# Revit family: Furniture_Sofas-Armchairs_HAGS_Armrest_sofa_armchair_couples
name_source: partatom
category: Furniture
revit_build: Autodesk Revit 2018 (Build: 20170223_1515(x64)
units: mm (PartAtom-declared; Revit-internal decimal feet)

## family parameters
Always vertical = Yes
Cut with Voids When Loaded = No
OmniClass Number = 23.21.23.13.15
OmniClass Title = Residential Sofas
Room Calculation Point = No
Shared = No
Work Plane-Based = No

## types (2) — shared parameters
BIMobject category = Sofas & Armchairs
Description = Armrest sofa / armchair couples
Edition number = 1
IFC Classification = Furniture
Manufacturer = Hags
Manufacturer name = HAGS
OmniClass Code = 23-21 23 13 15
OmniClass Description = Residential Sofas
Product Guid = e7462bcc-4176-425e-842d-c576c58401d0
Product SKU = Armrest_sofa_armchair_couples
Product data url = https://bimobject.com
Product name = Sofiero Armrest
Product url = https://hags.se
QR code = https://bimobject.com
URL = https://www.hags.com
Uniclass 1.4 Code = L8211
Uniclass 1.4 Description = Furniture

## per-type parameters (varying)
| type | Construction material | Model |
| 8037713 Black | Hags - Steel - Powder coated - Black | 8037713 |
| 8037714 Galvanized | Hags - Steel - Galvanized | 8037714 |

## geometry (parser evidence)
native form markers: Sweep x2
no freeform markers — native parametric forms only
